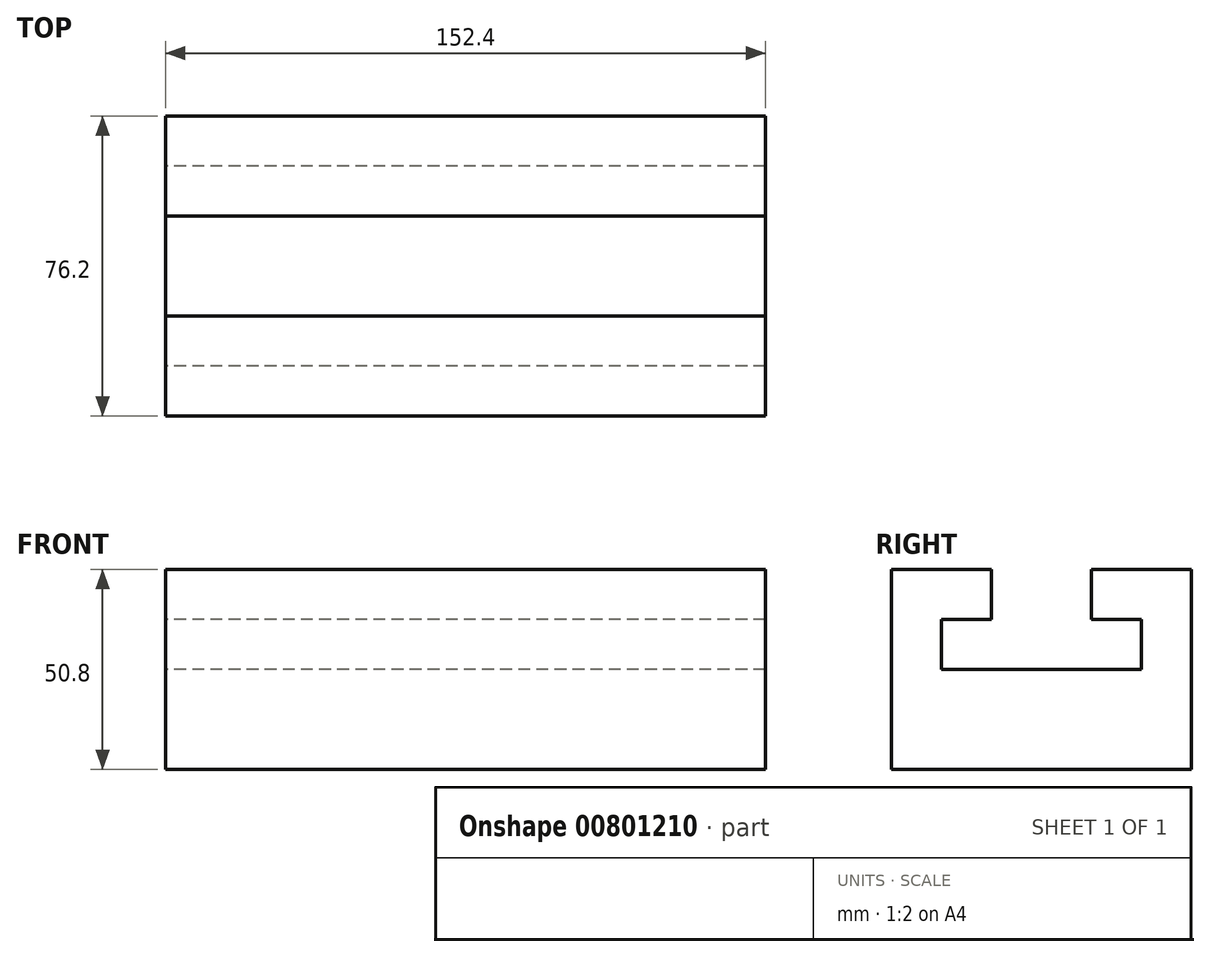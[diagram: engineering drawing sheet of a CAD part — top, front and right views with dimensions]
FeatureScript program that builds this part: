
annotation { "Feature Type Name" : "Feature", "Feature Type Description" : "" }
export const myFeature = defineFeature(function(context is Context, id is Id, definition is map)
    precondition{}
    {
        {
            var Q0;
            Q0=qCreatedBy(makeId("Right.planeOp"),FACE);
            var sketch = newSketch(context, id + "F0", { "sketchPlane" : qUnion([Q0])});
            skLineSegment(sketch, "E0", {"start": v(-40.15, -34.5) * mm, "end": v(36.05, -34.5) * mm});
            skLineSegment(sketch, "E1", {"start": v(36.05, -34.5) * mm, "end": v(36.05, 16.3) * mm});
            skLineSegment(sketch, "E2", {"start": v(36.05, 16.3) * mm, "end": v(10.65, 16.3) * mm});
            skLineSegment(sketch, "E3", {"start": v(10.65, 16.3) * mm, "end": v(10.65, 3.6) * mm});
            skLineSegment(sketch, "E4", {"start": v(10.65, 3.6) * mm, "end": v(23.35, 3.6) * mm});
            skLineSegment(sketch, "E5", {"start": v(23.35, 3.6) * mm, "end": v(23.35, -9.1) * mm});
            skLineSegment(sketch, "E6", {"start": v(23.35, -9.1) * mm, "end": v(-27.45, -9.1) * mm});
            skLineSegment(sketch, "E7", {"start": v(-27.45, -9.1) * mm, "end": v(-27.45, 3.6) * mm});
            skLineSegment(sketch, "E8", {"start": v(-27.45, 3.6) * mm, "end": v(-14.75, 3.6) * mm});
            skLineSegment(sketch, "E9", {"start": v(-14.75, 3.6) * mm, "end": v(-14.75, 16.3) * mm});
            skLineSegment(sketch, "E10", {"start": v(-14.75, 16.3) * mm, "end": v(-40.15, 16.3) * mm});
            skLineSegment(sketch, "E11", {"start": v(-40.15, 16.3) * mm, "end": v(-40.15, -34.5) * mm});
            skSolve(sketch);
        }
        {
            var Q0;
            Q0 = qSketchRegion(id + "F0", true);
            extrude(context, id + "F1", {"entities" : qUnion([Q0]), "depth" : 152.4 * mm, "offsetDistance" : 25.4 * mm});
        }
    });
